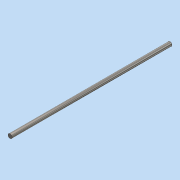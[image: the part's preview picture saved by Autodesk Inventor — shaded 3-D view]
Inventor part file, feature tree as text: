
AUTODESK INVENTOR PART (.ipt)
format: ipt  version: 2016 (Build 200138000, 138)  size: 82,944 bytes
history: native  units: mm
features: extrude x1, sketch x1
ambient origin geometry x8: Origin, YZ Plane, XZ Plane, XY Plane, X Axis, Y Axis, Z Axis, Center Point
bodies: Solid1 (feature_tree)
feature tree (2):
  extrude  "Extrusion1"  [1 undecoded]
  sketch  "Sketch1"  dims[d0=305.0mm d1=0.0mm]
note: 1 required parameter value undecoded (feature->parameter linkage not recoverable at this tier; creation-order binding heuristic only, values carry confidence <= 0.55)
